# Revit family: EHW217C
name_source: partatom
category: Plumbing Fixtures
units: mm (PartAtom-declared; Revit-internal decimal feet)

## family parameters
Always vertical = Yes
Cut with Voids When Loaded = No
OmniClass Number = 23.45.00.00
OmniClass Title = Sanitary, Laundry, and Cleaning Equipment
Part Type = Normal
Room Calculation Point = No
Round Connector Dimension = Use Diameter
Shared = No
Work Plane-Based = No

## types (4) — shared parameters
Activation by = Mechanical Front Bubbler Button
Assembly Code = D2010810
BODY_MATERIAL = Metal - Steel - Stainless - Chrome
BUBBLER_MATERIAL = Metal - Steel - Stainless - Chrome
BUTTON_MATERIAL = Metal - Steel - Stainless - Chrome
Bubbler Style = Vandal Resistant
CW Connection = Yes
Chilling Option = Non-refrigerated
DRAIN_MATERIAL = Metal - Steel - Stainless - Chrome
Description = Elkay Soft Sides Bi-Level Composite Fountain Non-Filtered, Non-Refrigerated White Granite Composite
Dimensions (L x W x H) = 38 1/2inch x 18 13/16inch x 20 3/8inch
Drain_Pipe 1 1/2" = 38 mm
Finish = WHT-White Granite Composite
HW Connection = No
Inlet pipe Higher Sink = 908 mm  [stored 2.979 ft]
Inlet pipe Lower Sink = 756 mm  [stored 2.48031 ft]
Inlet_Pipe = 10 mm  [stored 0.0328084 ft]
Installation Location = Indoor + Outdoor
Manufacturer = Elkay
Mounting Type = Wall Mount (On Wall)
No. of Stations Served = 2
SINK_MATERIAL = Metal - Steel - Stainless - Chrome
Special Feature = -
Vent Connection = No
Version = 1.0.0.0
Waste Connection = Yes

## per-type parameters (varying)
| type | Approx. Shipping Weight | Model |
| EHW217C | 61 lbs. | EHW217FPK |
| EHW217FPK | 91 lbs. | EHW217FPK |
| EHW217FPRAK | 91 lbs. | EHW217FPRAK |
| EHW217RAC | 70 lbs. | EHW217RAC |

note: [stored X ft] marks values corroborated as IEEE doubles in the binary element streams (Revit-internal decimal feet)

## geometry (parser evidence)
native form markers: Sweep x14
no freeform markers — native parametric forms only
